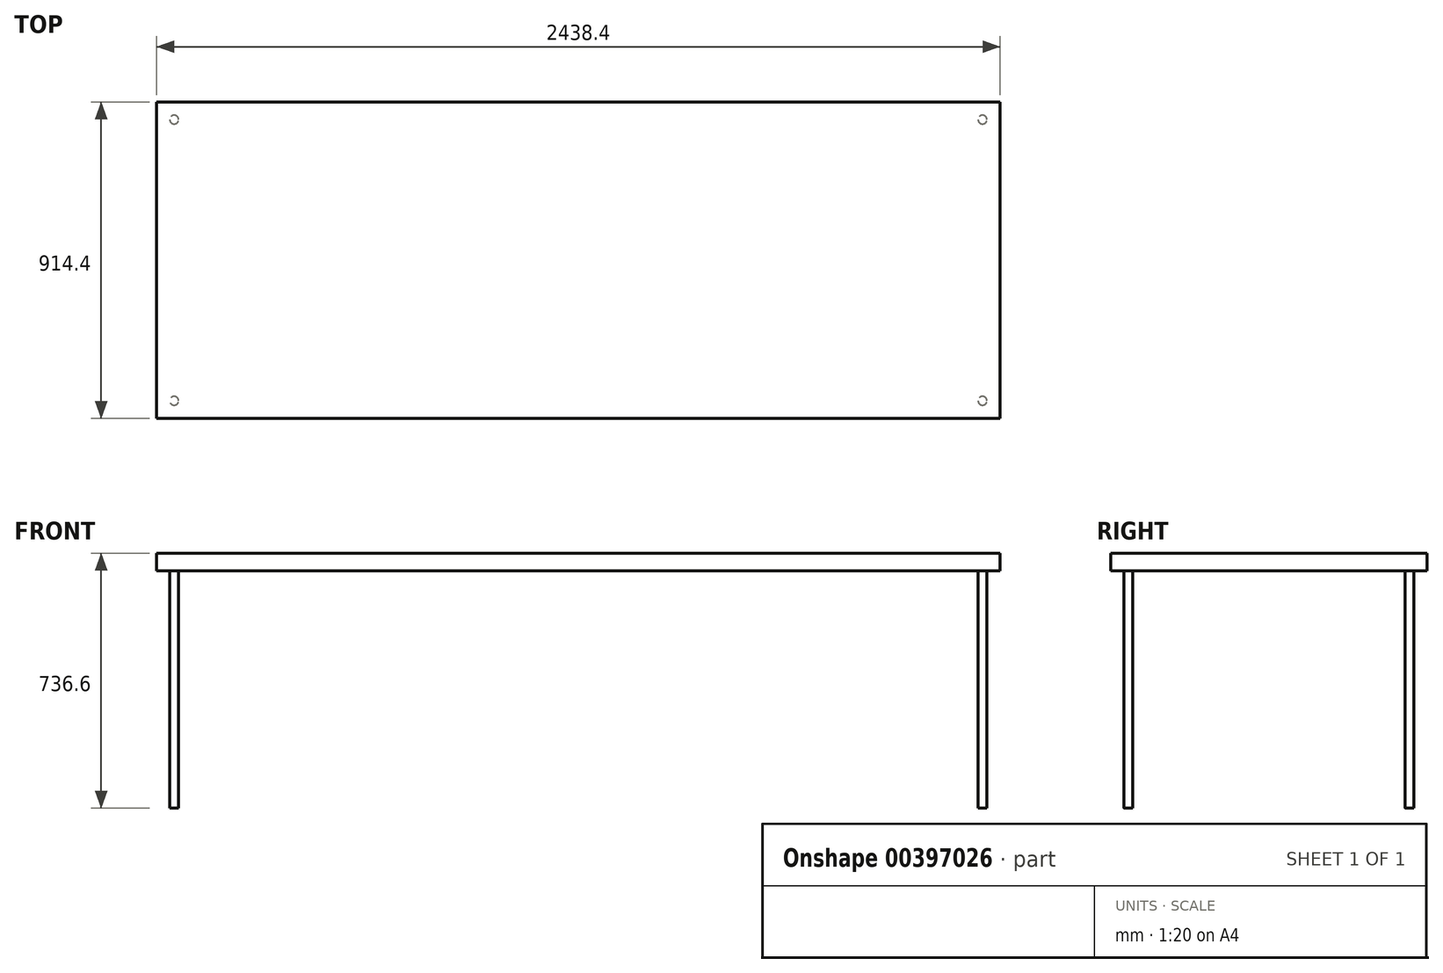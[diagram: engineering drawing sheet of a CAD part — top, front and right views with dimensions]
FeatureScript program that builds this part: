
annotation { "Feature Type Name" : "Feature", "Feature Type Description" : "" }
export const myFeature = defineFeature(function(context is Context, id is Id, definition is map)
    precondition{}
    {
        {
            var Q0;
            Q0=qCreatedBy(makeId("Top.planeOp"),FACE);
            var sketch = newSketch(context, id + "F0", { "sketchPlane" : qUnion([Q0])});
            skLineSegment(sketch, "E0.bottom", {"start": v(-1219.2, -457.2) * mm, "end": v(1219.2, -457.2) * mm});
            skLineSegment(sketch, "E0.top", {"start": v(-1219.2, 457.2) * mm, "end": v(1219.2, 457.2) * mm});
            skLineSegment(sketch, "E0.left", {"start": v(-1219.2, -457.2) * mm, "end": v(-1219.2, 457.2) * mm});
            skLineSegment(sketch, "E0.right", {"start": v(1219.2, -457.2) * mm, "end": v(1219.2, 457.2) * mm});
            skLineSegment(sketch, "E1", {"start": v(0, 457.2) * mm, "end": v(0, -457.2) * mm, "construction": true});
            skSolve(sketch);
        }
        {
            var Q0;
            Q0 = qSketchRegion(id + "F0", true);
            extrude(context, id + "F1", {"entities" : qUnion([Q0]), "depth" : 50.8 * mm});
        }
        {
            var Q0;
            Q0=makeQuery(id+"F1.opExtrude","CAP_FACE",FACE,{"disambiguationData":[OSD([sQuery(id+"F0.wireOp",EDGE,"E0.bottom"),sQuery(id+"F0.wireOp",EDGE,"E0.top"),sQuery(id+"F0.wireOp",EDGE,"E0.left"),sQuery(id+"F0.wireOp",EDGE,"E0.right")])],"isStart":true});
            var sketch = newSketch(context, id + "F2", { "sketchPlane" : qUnion([Q0])});
            skCircle(sketch, "E2", {"center": v(-1168.4, 406.4) * mm, "radius": 12.7 * mm});
            skCircle(sketch, "E3", {"center": v(-1168.4, -406.4) * mm, "radius": 12.7 * mm});
            skCircle(sketch, "E4", {"center": v(1168.4, -406.4) * mm, "radius": 12.7 * mm});
            skCircle(sketch, "E5", {"center": v(1168.4, 406.4) * mm, "radius": 12.7 * mm});
            skSolve(sketch);
        }
        {
            var Q0;
            Q0 = qSketchRegion(id + "F2", true);
            extrude(context, id + "F3", {"entities" : qUnion([Q0]), "operationType" : NewBodyOperationType.ADD, "depth" : 685.8 * mm});
        }
    });
